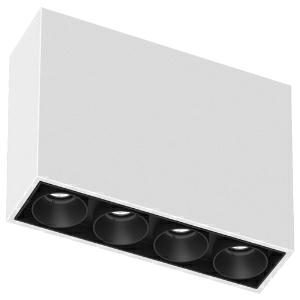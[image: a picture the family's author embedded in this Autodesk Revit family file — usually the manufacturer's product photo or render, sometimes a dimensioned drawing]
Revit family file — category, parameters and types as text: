
# Revit family: magiq_320-0710
name_source: partatom
category: Lighting Fixtures
units: mm (PartAtom-declared; Revit-internal decimal feet)

## family parameters
Cut with Voids When Loaded = No
Host = Face
Light Source = No
Part Type = Normal
Room Calculation Point = No
Round Connector Dimension = Use Diameter
Shared = No

## types (1)
- 320-0710-H27-U02-W11 (1 x LED, 880 lm, 13.3 W, 2700K)
    Apparent Load = 13 VA
    CIE Flux Codes = 98 99 99 100 75
    Color Rendering = 1A/90…99
    Color Temperature = 2700K
    Default Elevation = 1800 mm
    Description = MAGIQ
    Height = 110 mm
    Lamp = 1 x LED
    Lamp Light Flux = 880 lm
    Lamp Power = 13.3 W
    Lamp count = 1
    Length = 142 mm
    Luminous efficacy = 50 lm/W
    Manufacturer = Prolicht
    ModVariant = No
    Model = 320-0710
    Mounting Place = Ceiling
    Mounting Type = Surface mounted
    Number of Poles = 1
    OnlyDefault = Yes
    Power Factor = 1
    Product Name = MAGIQ
    Product group = Surface spotlights
    ProductGroupID = 332
    Protection Class = Protection class
    Protection Degree = Degree of protection
    RLX_Detail_Level = 1
    RlxData = <blob elided: 69501 chars, md5=6aadc311>
    Socket = socket
    Standby Power = 0 W
    System Light Flux = 659 lm
    System Power = 13 W
    Type Comments = LED COLOUR DIR 2700 K (27),FRAME_COLOUR BLACK (02),BEAMWIDTH Super Spot (11)
    Type Image = 320-0710.jpg
    URL = http://relux.com
    VarID = 320-0710-h27-u02-w11
    Voltage = 0 V
    Weight = 0.00 kg
    Width = 42 mm

## geometry (parser evidence)
native form markers: Blend x4, Sweep x10
no freeform markers — native parametric forms only
